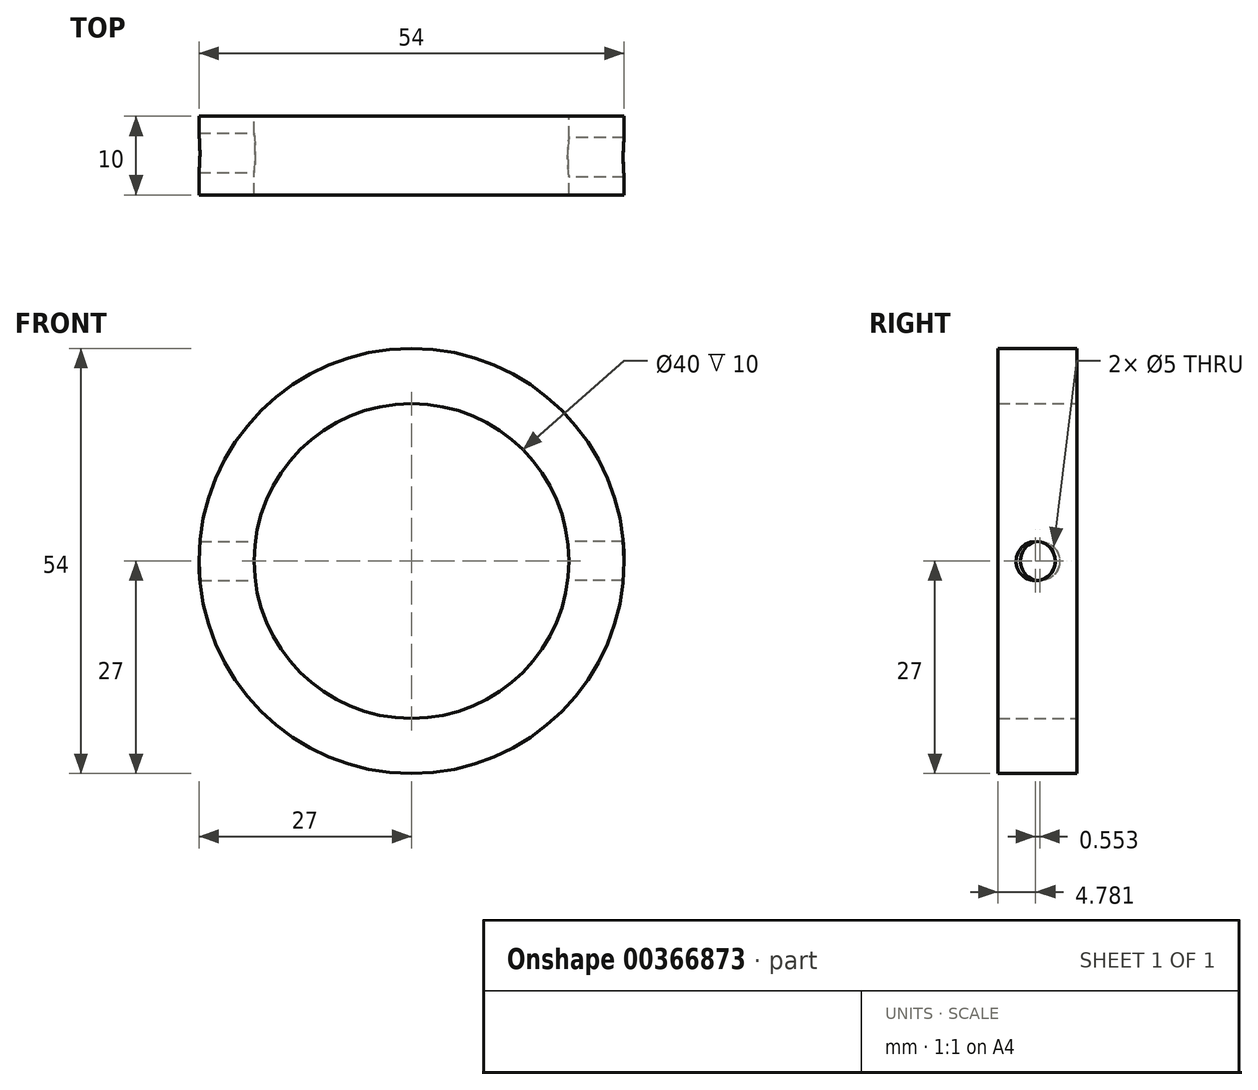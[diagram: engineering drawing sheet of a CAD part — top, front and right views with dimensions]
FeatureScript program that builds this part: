
annotation { "Feature Type Name" : "Feature", "Feature Type Description" : "" }
export const myFeature = defineFeature(function(context is Context, id is Id, definition is map)
    precondition{}
    {
        {
            var Q0;
            Q0=qCreatedBy(makeId("Front.planeOp"),FACE);
            var sketch = newSketch(context, id + "F0", { "sketchPlane" : qUnion([Q0])});
            skCircle(sketch, "E0", {"center": v(0, 0) * mm, "radius": 27 * mm});
            skCircle(sketch, "E1", {"center": v(0, 0) * mm, "radius": 20 * mm});
            skSolve(sketch);
        }
        {
            var Q0;
            Q0=makeQuery(id+"F0.imprint","IMPRINT",FACE,{"disambiguationData":[TD([[makeQuery(id+"F0.imprint","IMPRINT",EDGE,{"derivedFrom":sQuery(id+"F0.wireOp",EDGE,"E0")}),1.0]])]});
            extrude(context, id + "F1", {"entities" : qUnion([Q0]), "depth" : 10 * mm});
        }
        {
            var Q0;
            Q0=qCreatedBy(makeId("Right.planeOp"),FACE);
            var sketch = newSketch(context, id + "F2", { "sketchPlane" : qUnion([Q0])});
            skPoint(sketch, "E2", {"position": v(-4.67, 0) * mm});
            skSolve(sketch);
        }
        {
            var Q0;
            Q0=sQuery(id+"F2.wireOp",VERTEX,"E2");
            var Q1;
            Q1=makeQuery(id+"F1.opExtrude","SWEPT_BODY",BODY,{"disambiguationData":[OSD([sQuery(id+"F0.wireOp",EDGE,"E0"),sQuery(id+"F0.wireOp",EDGE,"E1")])]});
            hole(context, id + "F3", {"style" : HoleStyle.SIMPLE, "endStyle" : HoleEndStyle.THROUGH, "holeDiameter" : 5 * mm, "isTappedThrough" : true, "tappedDepth" : 12 * mm, "tapClearance" : 3, "locations" : qUnion([Q0]), "scope" : qUnion([Q1])});
        }
        {
            var Q0;
            Q0=qCreatedBy(makeId("Right.planeOp"),FACE);
            var sketch = newSketch(context, id + "F4", { "sketchPlane" : qUnion([Q0])});
            skPoint(sketch, "E3", {"position": v(-5.22, 0) * mm});
            skSolve(sketch);
        }
        {
            var Q0;
            Q0=sQuery(id+"F4.wireOp",VERTEX,"E3");
            var Q1;
            Q1=makeQuery(id+"F1.opExtrude","SWEPT_BODY",BODY,{"disambiguationData":[OSD([sQuery(id+"F0.wireOp",EDGE,"E0"),sQuery(id+"F0.wireOp",EDGE,"E1")])]});
            hole(context, id + "F5", {"style" : HoleStyle.SIMPLE, "endStyle" : HoleEndStyle.THROUGH, "oppositeDirection" : true, "holeDiameter" : 5 * mm, "isTappedThrough" : true, "tappedDepth" : 12 * mm, "tapClearance" : 3, "locations" : qUnion([Q0]), "scope" : qUnion([Q1])});
        }
    });
